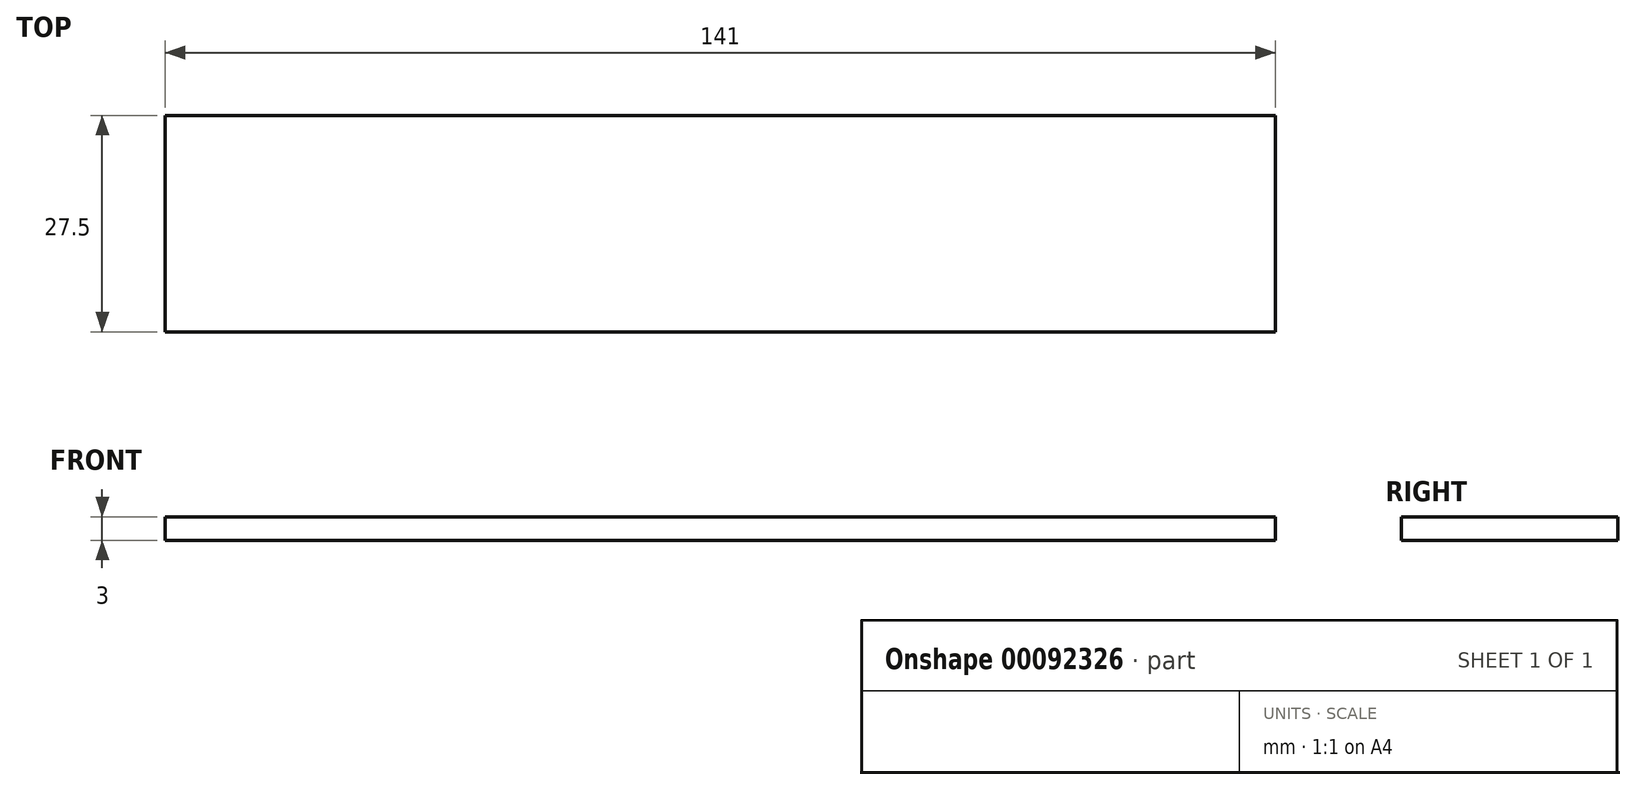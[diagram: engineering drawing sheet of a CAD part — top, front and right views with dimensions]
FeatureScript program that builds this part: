
annotation { "Feature Type Name" : "Feature", "Feature Type Description" : "" }
export const myFeature = defineFeature(function(context is Context, id is Id, definition is map)
    precondition{}
    {
        {
            var Q0;
            Q0=qCreatedBy(makeId("Top.planeOp"),FACE);
            var sketch = newSketch(context, id + "F0", { "sketchPlane" : qUnion([Q0])});
            skLineSegment(sketch, "E0.bottom", {"start": v(-70.5, 13.75) * mm, "end": v(70.5, 13.75) * mm});
            skLineSegment(sketch, "E0.top", {"start": v(-70.5, -13.75) * mm, "end": v(70.5, -13.75) * mm});
            skLineSegment(sketch, "E0.left", {"start": v(-70.5, 13.75) * mm, "end": v(-70.5, -13.75) * mm});
            skLineSegment(sketch, "E0.right", {"start": v(70.5, 13.75) * mm, "end": v(70.5, -13.75) * mm});
            skSolve(sketch);
        }
        {
            var Q0;
            Q0=makeQuery(id+"F0.imprint","IMPRINT",FACE,{"disambiguationData":[TD([[makeQuery(id+"F0.imprint","IMPRINT",EDGE,{"derivedFrom":sQuery(id+"F0.wireOp",EDGE,"E0.bottom")}),-1.0]])]});
            extrude(context, id + "F1", {"entities" : qUnion([Q0]), "endBound" : BoundingType.SYMMETRIC, "depth" : 3 * mm});
        }
    });
